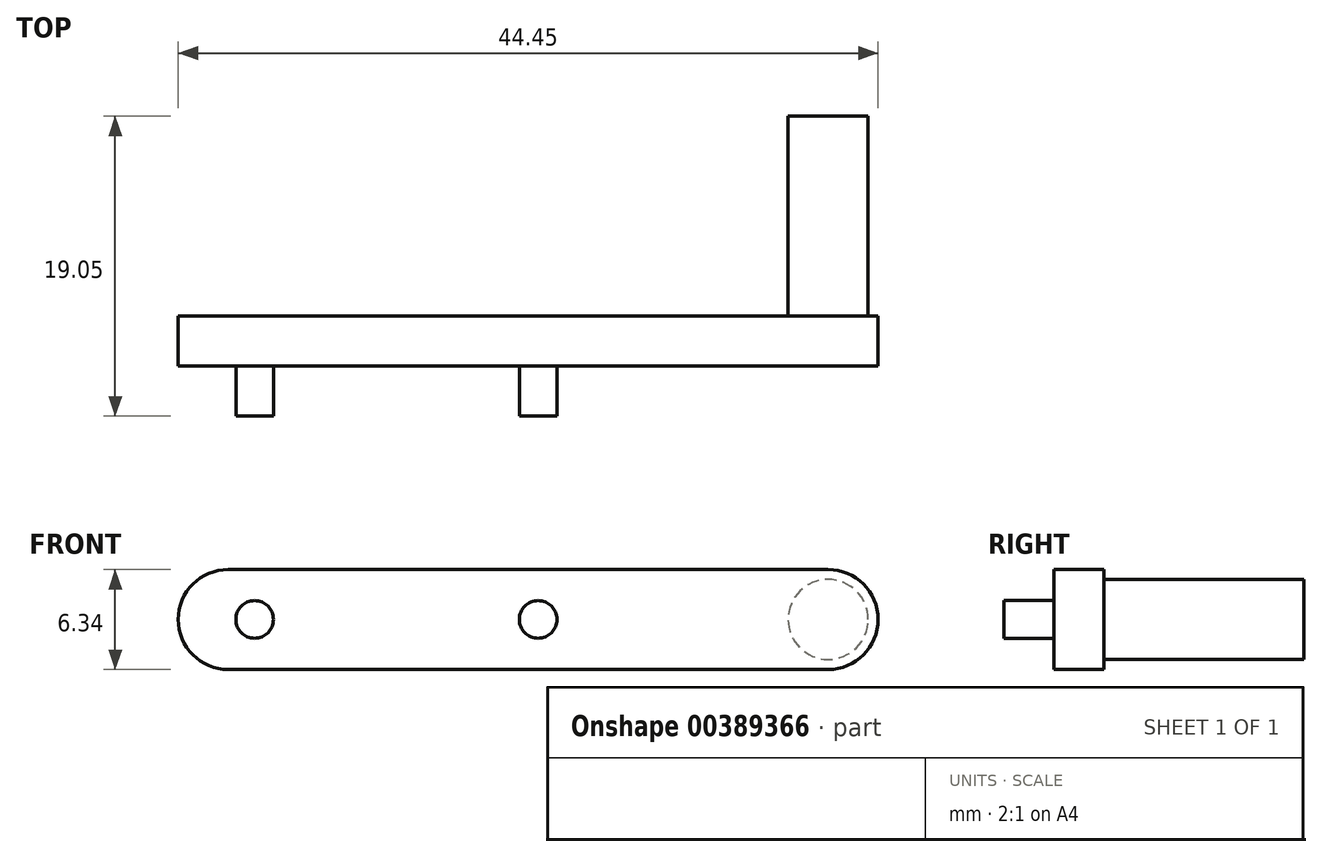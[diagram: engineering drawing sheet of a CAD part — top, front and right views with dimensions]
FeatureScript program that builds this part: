
annotation { "Feature Type Name" : "Feature", "Feature Type Description" : "" }
export const myFeature = defineFeature(function(context is Context, id is Id, definition is map)
    precondition{}
    {
        {
            var Q0;
            Q0=qCreatedBy(makeId("Front.planeOp"),FACE);
            var sketch = newSketch(context, id + "F0", { "sketchPlane" : qUnion([Q0])});
            skCircle(sketch, "E0", {"center": v(-60.86, 0) * mm, "radius": 3.18 * mm});
            skCircle(sketch, "E1", {"center": v(-22.76, 0) * mm, "radius": 3.18 * mm});
            skLineSegment(sketch, "E2", {"start": v(-60.86, 3.18) * mm, "end": v(-22.76, 3.18) * mm});
            skLineSegment(sketch, "E3", {"start": v(-60.86, -3.18) * mm, "end": v(-22.76, -3.18) * mm});
            skSolve(sketch);
        }
        {
            var Q0;
            Q0 = qSketchRegion(id + "F0", true);
            extrude(context, id + "F1", {"entities" : qUnion([Q0]), "depth" : 3.17 * mm});
        }
        {
            var Q0;
            Q0=makeQuery(id+"F1.opExtrude","CAP_FACE",FACE,{"disambiguationData":[OSD([sQuery(id+"F0.wireOp",EDGE,"E0"),sQuery(id+"F0.wireOp",EDGE,"E1"),sQuery(id+"F0.wireOp",EDGE,"E2"),sQuery(id+"F0.wireOp",EDGE,"E3")])],"isStart":false});
            var sketch = newSketch(context, id + "F2", { "sketchPlane" : qUnion([Q0])});
            skCircle(sketch, "E4", {"center": v(-41.18, 0) * mm, "radius": 1.2 * mm});
            skCircle(sketch, "E5", {"center": v(-59.19, 0) * mm, "radius": 1.2 * mm});
            skSolve(sketch);
        }
        {
            var Q0;
            Q0 = qSketchRegion(id + "F2", true);
            extrude(context, id + "F3", {"entities" : qUnion([Q0]), "operationType" : NewBodyOperationType.ADD, "depth" : 3.17 * mm});
        }
        {
            var Q0;
            Q0=makeQuery(id+"F1.opExtrude","CAP_FACE",FACE,{"disambiguationData":[OSD([sQuery(id+"F0.wireOp",EDGE,"E0"),sQuery(id+"F0.wireOp",EDGE,"E1"),sQuery(id+"F0.wireOp",EDGE,"E2"),sQuery(id+"F0.wireOp",EDGE,"E3")])],"isStart":true});
            var sketch = newSketch(context, id + "F4", { "sketchPlane" : qUnion([Q0])});
            skCircle(sketch, "E6", {"center": v(22.76, 0) * mm, "radius": 2.54 * mm});
            skSolve(sketch);
        }
        {
            var Q0;
            Q0 = qSketchRegion(id + "F4", true);
            extrude(context, id + "F5", {"entities" : qUnion([Q0]), "operationType" : NewBodyOperationType.ADD, "depth" : 12.7 * mm});
        }
    });
